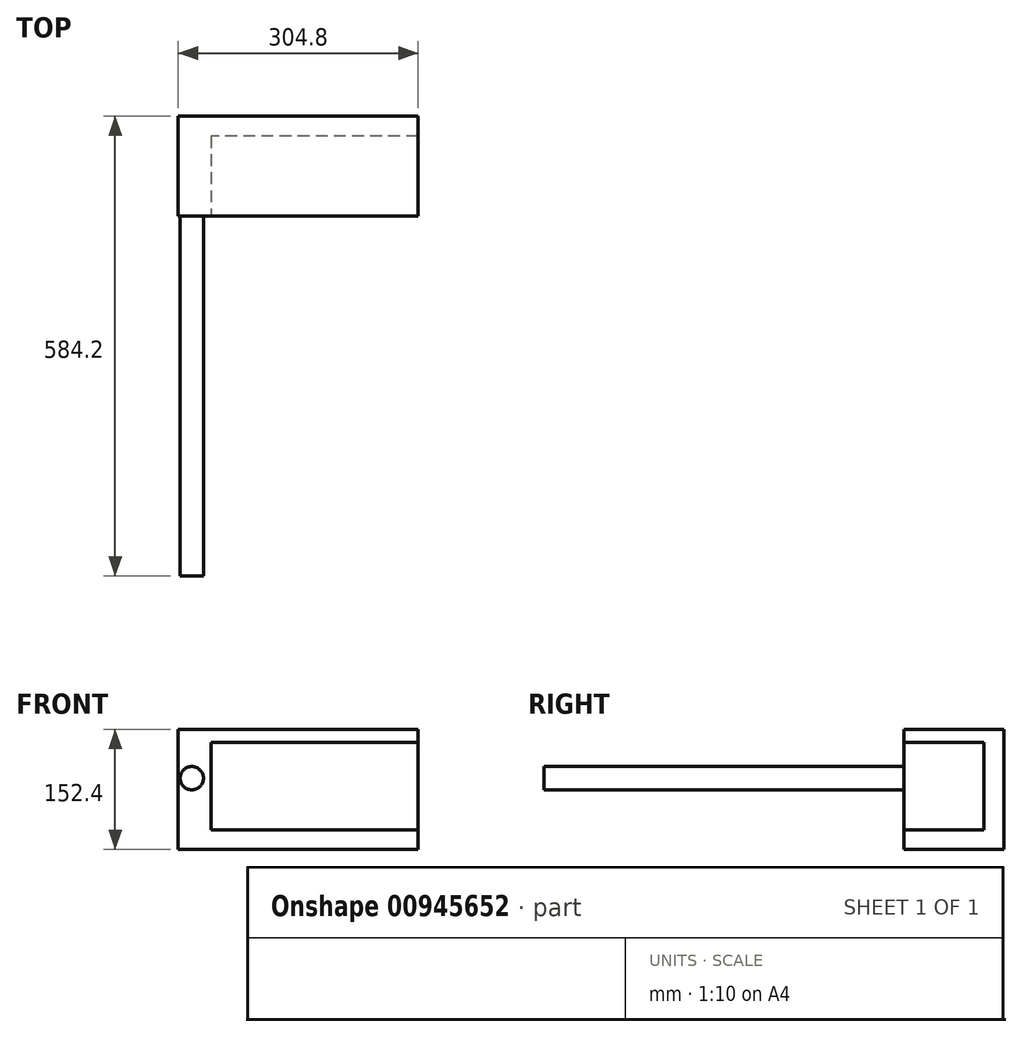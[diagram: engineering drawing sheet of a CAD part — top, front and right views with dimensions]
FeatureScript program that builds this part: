
annotation { "Feature Type Name" : "Feature", "Feature Type Description" : "" }
export const myFeature = defineFeature(function(context is Context, id is Id, definition is map)
    precondition{}
    {
        {
            var Q0;
            Q0=qCreatedBy(makeId("Front.planeOp"),FACE);
            var sketch = newSketch(context, id + "F0", { "sketchPlane" : qUnion([Q0])});
            skLineSegment(sketch, "E0.bottom", {"start": v(152.4, -76.2) * mm, "end": v(-152.4, -76.2) * mm});
            skLineSegment(sketch, "E0.top", {"start": v(152.4, 76.2) * mm, "end": v(-152.4, 76.2) * mm});
            skLineSegment(sketch, "E0.left", {"start": v(152.4, -76.2) * mm, "end": v(152.4, 76.2) * mm});
            skLineSegment(sketch, "E0.right", {"start": v(-152.4, -76.2) * mm, "end": v(-152.4, 76.2) * mm});
            skPoint(sketch, "E0.middle", {"position": v(0, 0) * mm});
            skSolve(sketch);
        }
        {
            var Q0;
            Q0=qSketchRegion(id+"F0",true);
            extrude(context, id + "F1", {"entities" : qUnion([Q0]), "depth" : 127 * mm, "offsetDistance" : 25.4 * mm});
        }
        {
            var Q0;
            Q0=makeQuery(id+"F1.opExtrude","CAP_FACE",FACE,{"disambiguationData":[OSD([sQuery(id+"F0.wireOp",EDGE,"E0.bottom"),sQuery(id+"F0.wireOp",EDGE,"E0.top"),sQuery(id+"F0.wireOp",EDGE,"E0.left"),sQuery(id+"F0.wireOp",EDGE,"E0.right")])],"isStart":false});
            var sketch = newSketch(context, id + "F2", { "sketchPlane" : qUnion([Q0])});
            skLineSegment(sketch, "E1.bottom", {"start": v(152.4, 60.03) * mm, "end": v(-110.36, 60.03) * mm});
            skLineSegment(sketch, "E1.top", {"start": v(152.4, -51.7) * mm, "end": v(-110.36, -51.7) * mm});
            skLineSegment(sketch, "E1.left", {"start": v(152.4, 60.03) * mm, "end": v(152.4, -51.7) * mm});
            skLineSegment(sketch, "E1.right", {"start": v(-110.36, 60.03) * mm, "end": v(-110.36, -51.7) * mm});
            skSolve(sketch);
        }
        {
            var Q0;
            Q0=qSketchRegion(id+"F2",true);
            extrude(context, id + "F3", {"entities" : qUnion([Q0]), "operationType" : NewBodyOperationType.REMOVE, "endBound" : BoundingType.SYMMETRIC, "oppositeDirection" : true, "depth" : 203.2 * mm, "offsetDistance" : 25.4 * mm});
        }
        {
            var Q0;
            Q0=makeQuery(id+"F1.opExtrude","CAP_FACE",FACE,{"disambiguationData":[OSD([sQuery(id+"F0.wireOp",EDGE,"E0.bottom"),sQuery(id+"F0.wireOp",EDGE,"E0.top"),sQuery(id+"F0.wireOp",EDGE,"E0.left"),sQuery(id+"F0.wireOp",EDGE,"E0.right")])],"isStart":false});
            var sketch = newSketch(context, id + "F4", { "sketchPlane" : qUnion([Q0])});
            skCircle(sketch, "E2", {"center": v(-135.15, 14.28) * mm, "radius": 14.82 * mm});
            skSolve(sketch);
        }
        {
            var Q0;
            Q0=makeQuery(id+"F4.imprint","IMPRINT",FACE,{"disambiguationData":[TD([[makeQuery(id+"F4.imprint","IMPRINT",EDGE,{"derivedFrom":sQuery(id+"F4.wireOp",EDGE,"E2")}),1.0]])]});
            extrude(context, id + "F5", {"entities" : qUnion([Q0]), "operationType" : NewBodyOperationType.ADD, "depth" : 457.2 * mm, "offsetDistance" : 25.4 * mm});
        }
    });
